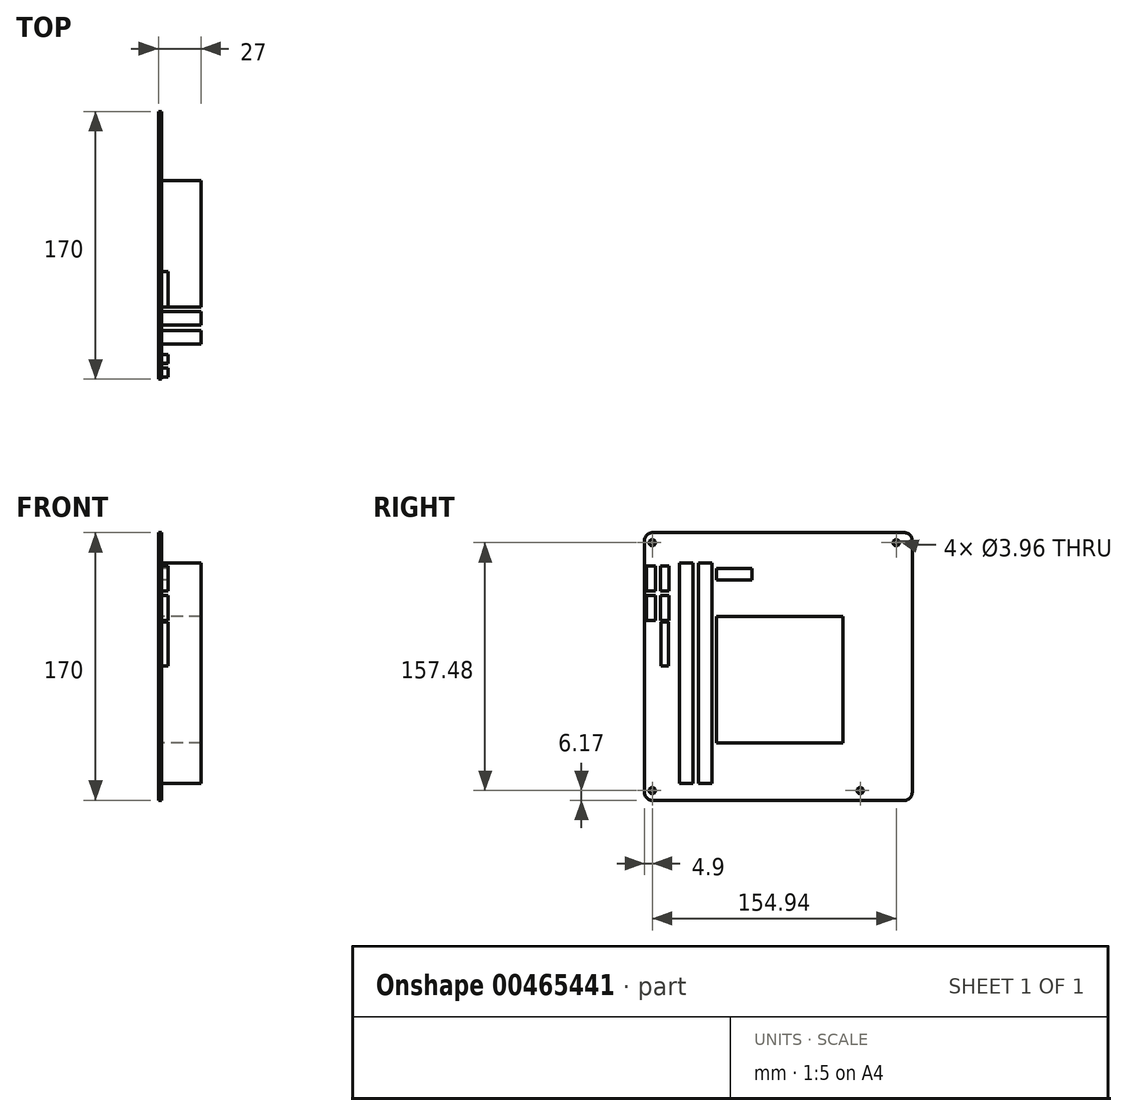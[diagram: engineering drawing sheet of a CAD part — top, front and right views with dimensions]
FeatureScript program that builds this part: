
annotation { "Feature Type Name" : "Feature", "Feature Type Description" : "" }
export const myFeature = defineFeature(function(context is Context, id is Id, definition is map)
    precondition{}
    {
        {
            var Q0;
            Q0=qCreatedBy(makeId("Right.planeOp"),FACE);
            var sketch = newSketch(context, id + "F0", { "sketchPlane" : qUnion([Q0])});
            skLineSegment(sketch, "E0.bottom", {"start": v(80, -85) * mm, "end": v(-80, -85) * mm});
            skLineSegment(sketch, "E0.top", {"start": v(80, 85) * mm, "end": v(-80, 85) * mm});
            skLineSegment(sketch, "E0.left", {"start": v(85, -80) * mm, "end": v(85, 80) * mm});
            skLineSegment(sketch, "E0.right", {"start": v(-85, -80) * mm, "end": v(-85, 80) * mm});
            skPoint(sketch, "E0.middle", {"position": v(0, 0) * mm});
            skLineSegment(sketch, "E1", {"start": v(-78.65, 78.84) * mm, "end": v(-78.65, -84.1) * mm, "construction": true});
            skLineSegment(sketch, "E2", {"start": v(-82.65, 74.84) * mm, "end": v(-47.92, 74.84) * mm, "construction": true});
            skCircle(sketch, "E3", {"center": v(-78.65, 74.84) * mm, "radius": 1.98 * mm});
            skLineSegment(sketch, "E4", {"start": v(-82.65, -80.1) * mm, "end": v(82.83, -80.1) * mm, "construction": true});
            skLineSegment(sketch, "E5", {"start": v(78.83, -84.1) * mm, "end": v(78.83, 55.98) * mm, "construction": true});
            skLineSegment(sketch, "E6", {"start": v(82.83, 51.98) * mm, "end": v(62.83, 51.98) * mm, "construction": true});
            skCircle(sketch, "E7", {"center": v(-78.65, -80.1) * mm, "radius": 1.98 * mm});
            skCircle(sketch, "E8", {"center": v(78.83, -80.1) * mm, "radius": 1.98 * mm});
            skCircle(sketch, "E9", {"center": v(78.83, 51.98) * mm, "radius": 1.98 * mm});
            skPoint(sketch, "E10.visualSharp", {"position": v(-85, -85) * mm});
            skArc(sketch, "E10.filletArc", {"start": v(-85, -80) * mm, "mid": v(-83.54, -83.54) * mm, "end": v(-80, -85) * mm});
            skPoint(sketch, "E11.visualSharp", {"position": v(85, -85) * mm});
            skArc(sketch, "E11.filletArc", {"start": v(80, -85) * mm, "mid": v(83.54, -83.54) * mm, "end": v(85, -80) * mm});
            skPoint(sketch, "E12.visualSharp", {"position": v(85, 85) * mm});
            skArc(sketch, "E12.filletArc", {"start": v(85, 80) * mm, "mid": v(83.54, 83.54) * mm, "end": v(80, 85) * mm});
            skPoint(sketch, "E13.visualSharp", {"position": v(-85, 85) * mm});
            skArc(sketch, "E13.filletArc", {"start": v(-80, 85) * mm, "mid": v(-83.54, 83.54) * mm, "end": v(-85, 80) * mm});
            skSolve(sketch);
        }
        {
            var Q0;
            Q0 = qSketchRegion(id + "F0", true);
            extrude(context, id + "F1", {"entities" : qUnion([Q0]), "depth" : 2 * mm});
        }
        {
            var Q0;
            Q0=qCreatedBy(makeId("Top.planeOp"),FACE);
            var sketch = newSketch(context, id + "F2", { "sketchPlane" : qUnion([Q0])});
            skLineSegment(sketch, "E14", {"start": v(-62.53, 0) * mm, "end": v(64.7, 0) * mm, "construction": true});
            skSolve(sketch);
        }
        {
            var Q0;
            Q0=makeQuery(id+"F1.opExtrude","SWEPT_BODY",BODY,{"disambiguationData":[OSD([sQuery(id+"F0.wireOp",EDGE,"E0.bottom"),sQuery(id+"F0.wireOp",EDGE,"E0.top"),sQuery(id+"F0.wireOp",EDGE,"E0.left"),sQuery(id+"F0.wireOp",EDGE,"E0.right"),sQuery(id+"F0.wireOp",EDGE,"E3"),sQuery(id+"F0.wireOp",EDGE,"E7"),sQuery(id+"F0.wireOp",EDGE,"E8"),sQuery(id+"F0.wireOp",EDGE,"E9"),sQuery(id+"F0.wireOp",EDGE,"E10.filletArc"),sQuery(id+"F0.wireOp",EDGE,"E11.filletArc"),sQuery(id+"F0.wireOp",EDGE,"E12.filletArc"),sQuery(id+"F0.wireOp",EDGE,"E13.filletArc")])]});
            var Q1;
            Q1=sQuery(id+"F2.wireOp",EDGE,"E14");
            transform(context, id + "F3", {"entities" : qUnion([Q0]), "transformType" : TransformType.ROTATION, "transformAxis" : qUnion([Q1]), "angle" : 90 * degree, "oppositeDirection" : true, "makeCopy" : false});
        }
        {
            var Q0;
            Q0=makeQuery(id+"F1.opExtrude","CAP_FACE",FACE,{"disambiguationData":[OSD([sQuery(id+"F0.wireOp",EDGE,"E0.bottom"),sQuery(id+"F0.wireOp",EDGE,"E0.top"),sQuery(id+"F0.wireOp",EDGE,"E0.left"),sQuery(id+"F0.wireOp",EDGE,"E0.right"),sQuery(id+"F0.wireOp",EDGE,"E3"),sQuery(id+"F0.wireOp",EDGE,"E7"),sQuery(id+"F0.wireOp",EDGE,"E8"),sQuery(id+"F0.wireOp",EDGE,"E9"),sQuery(id+"F0.wireOp",EDGE,"E10.filletArc"),sQuery(id+"F0.wireOp",EDGE,"E11.filletArc"),sQuery(id+"F0.wireOp",EDGE,"E12.filletArc"),sQuery(id+"F0.wireOp",EDGE,"E13.filletArc")])],"isStart":false});
            var sketch = newSketch(context, id + "F4", { "sketchPlane" : qUnion([Q0])});
            skLineSegment(sketch, "E15.0", {"start": v(-80, 85) * mm, "end": v(80, 85) * mm, "construction": true});
            skLineSegment(sketch, "E16.0", {"start": v(-80, -85) * mm, "end": v(80, -85) * mm, "construction": true});
            skLineSegment(sketch, "E17.0", {"start": v(-85, -80) * mm, "end": v(-85, 80) * mm, "construction": true});
            skLineSegment(sketch, "E18.bottom", {"start": v(-69.94, 28.22) * mm, "end": v(-74.55, 28.22) * mm});
            skLineSegment(sketch, "E18.top", {"start": v(-69.94, 0.5) * mm, "end": v(-74.55, 0.5) * mm});
            skLineSegment(sketch, "E18.left", {"start": v(-69.94, 28.22) * mm, "end": v(-69.94, 0.5) * mm});
            skLineSegment(sketch, "E18.right", {"start": v(-74.55, 28.22) * mm, "end": v(-74.55, 0.5) * mm});
            skLineSegment(sketch, "E19", {"start": v(-68.5, 46.63) * mm, "end": v(-83.45, 46.63) * mm, "construction": true});
            skLineSegment(sketch, "E20", {"start": v(-76.5, 64.43) * mm, "end": v(-76.5, 28.91) * mm, "construction": true});
            skLineSegment(sketch, "E21.bottom", {"start": v(-75, 47.98) * mm, "end": v(-69.36, 47.98) * mm});
            skLineSegment(sketch, "E21.top", {"start": v(-75, 63.86) * mm, "end": v(-69.36, 63.86) * mm});
            skLineSegment(sketch, "E21.left", {"start": v(-75, 47.98) * mm, "end": v(-75, 63.86) * mm});
            skLineSegment(sketch, "E21.right", {"start": v(-69.36, 47.98) * mm, "end": v(-69.36, 63.86) * mm});
            skLineSegment(sketch, "E22.MirrorCS", {"start": v(-83.64, 47.98) * mm, "end": v(-83.64, 63.86) * mm});
            skLineSegment(sketch, "E23.MirrorCS", {"start": v(-78, 63.86) * mm, "end": v(-83.64, 63.86) * mm});
            skLineSegment(sketch, "E24.MirrorCS", {"start": v(-78, 47.98) * mm, "end": v(-83.64, 47.98) * mm});
            skLineSegment(sketch, "E25.MirrorCS", {"start": v(-78, 47.98) * mm, "end": v(-78, 63.86) * mm});
            skLineSegment(sketch, "E26.MirrorCS", {"start": v(-78, 29.4) * mm, "end": v(-83.64, 29.4) * mm});
            skLineSegment(sketch, "E27.MirrorCS", {"start": v(-78, 45.28) * mm, "end": v(-83.64, 45.28) * mm});
            skLineSegment(sketch, "E28.MirrorCS", {"start": v(-75, 45.28) * mm, "end": v(-75, 29.4) * mm});
            skLineSegment(sketch, "E29.MirrorCS", {"start": v(-75, 45.28) * mm, "end": v(-69.36, 45.28) * mm});
            skLineSegment(sketch, "E30.MirrorCS", {"start": v(-69.36, 45.28) * mm, "end": v(-69.36, 29.4) * mm});
            skLineSegment(sketch, "E31.MirrorCS", {"start": v(-83.64, 45.28) * mm, "end": v(-83.64, 29.4) * mm});
            skLineSegment(sketch, "E32.MirrorCS", {"start": v(-78, 45.28) * mm, "end": v(-78, 29.4) * mm});
            skLineSegment(sketch, "E33.MirrorCS", {"start": v(-75, 29.4) * mm, "end": v(-69.36, 29.4) * mm});
            skLineSegment(sketch, "E34.bottom", {"start": v(-16.74, 55.01) * mm, "end": v(-39.27, 55.01) * mm});
            skLineSegment(sketch, "E34.top", {"start": v(-16.74, 62.4) * mm, "end": v(-39.27, 62.4) * mm});
            skLineSegment(sketch, "E34.left", {"start": v(-16.74, 55.01) * mm, "end": v(-16.74, 62.4) * mm});
            skLineSegment(sketch, "E34.right", {"start": v(-39.27, 55.01) * mm, "end": v(-39.27, 62.4) * mm});
            skLineSegment(sketch, "E35.bottom", {"start": v(41.01, 31.65) * mm, "end": v(-39.33, 31.65) * mm});
            skLineSegment(sketch, "E35.top", {"start": v(41.01, -48.47) * mm, "end": v(-39.33, -48.47) * mm});
            skLineSegment(sketch, "E35.left", {"start": v(41.01, 31.65) * mm, "end": v(41.01, -48.47) * mm});
            skLineSegment(sketch, "E35.right", {"start": v(-39.33, 31.65) * mm, "end": v(-39.33, -48.47) * mm});
            skLineSegment(sketch, "E36.bottom", {"start": v(-42.06, 65.73) * mm, "end": v(-50.68, 65.73) * mm});
            skLineSegment(sketch, "E36.top", {"start": v(-42.06, -74.29) * mm, "end": v(-50.68, -74.29) * mm});
            skLineSegment(sketch, "E36.left", {"start": v(-42.06, 65.73) * mm, "end": v(-42.06, -74.29) * mm});
            skLineSegment(sketch, "E36.right", {"start": v(-50.68, 65.73) * mm, "end": v(-50.68, -74.29) * mm});
            skLineSegment(sketch, "E37", {"start": v(-52.4, 69.79) * mm, "end": v(-52.4, -78.07) * mm, "construction": true});
            skLineSegment(sketch, "E38.MirrorCS", {"start": v(-54.11, 65.73) * mm, "end": v(-54.11, -74.29) * mm});
            skLineSegment(sketch, "E39.MirrorCS", {"start": v(-62.73, 65.73) * mm, "end": v(-54.11, 65.73) * mm});
            skLineSegment(sketch, "E40.MirrorCS", {"start": v(-62.73, 65.73) * mm, "end": v(-62.73, -74.29) * mm});
            skLineSegment(sketch, "E41.MirrorCS", {"start": v(-62.73, -74.29) * mm, "end": v(-54.11, -74.29) * mm});
            skSolve(sketch);
        }
        {
            var Q0;
            Q0=makeQuery(id+"F4.imprint","IMPRINT",FACE,{"disambiguationData":[TD([[makeQuery(id+"F4.imprint","IMPRINT",EDGE,{"derivedFrom":sQuery(id+"F4.wireOp",EDGE,"E21.bottom")}),1.0]])]});
            var Q1;
            Q1=makeQuery(id+"F4.imprint","IMPRINT",FACE,{"disambiguationData":[TD([[makeQuery(id+"F4.imprint","IMPRINT",EDGE,{"derivedFrom":sQuery(id+"F4.wireOp",EDGE,"E22.MirrorCS")}),-1.0]])]});
            var Q2;
            Q2=makeQuery(id+"F4.imprint","IMPRINT",FACE,{"disambiguationData":[TD([[makeQuery(id+"F4.imprint","IMPRINT",EDGE,{"derivedFrom":sQuery(id+"F4.wireOp",EDGE,"E26.MirrorCS")}),-1.0]])]});
            var Q3;
            Q3=makeQuery(id+"F4.imprint","IMPRINT",FACE,{"disambiguationData":[TD([[makeQuery(id+"F4.imprint","IMPRINT",EDGE,{"derivedFrom":sQuery(id+"F4.wireOp",EDGE,"E28.MirrorCS")}),1.0]])]});
            extrude(context, id + "F5", {"entities" : qUnion([Q0, Q1, Q2, Q3]), "operationType" : NewBodyOperationType.ADD, "depth" : 4 * mm});
        }
        {
            var Q0;
            Q0=makeQuery(id+"F4.imprint","IMPRINT",FACE,{"disambiguationData":[TD([[makeQuery(id+"F4.imprint","IMPRINT",EDGE,{"derivedFrom":sQuery(id+"F4.wireOp",EDGE,"E18.bottom")}),1.0]])]});
            extrude(context, id + "F6", {"entities" : qUnion([Q0]), "operationType" : NewBodyOperationType.ADD, "depth" : 4 * mm});
        }
        {
            var Q0;
            Q0=makeQuery(id+"F4.imprint","IMPRINT",FACE,{"disambiguationData":[TD([[makeQuery(id+"F4.imprint","IMPRINT",EDGE,{"derivedFrom":sQuery(id+"F4.wireOp",EDGE,"E34.bottom")}),-1.0]])]});
            extrude(context, id + "F7", {"entities" : qUnion([Q0]), "operationType" : NewBodyOperationType.ADD, "depth" : 4 * mm});
        }
        {
            var Q0;
            Q0=makeQuery(id+"F4.imprint","IMPRINT",FACE,{"disambiguationData":[TD([[makeQuery(id+"F4.imprint","IMPRINT",EDGE,{"derivedFrom":sQuery(id+"F4.wireOp",EDGE,"E35.bottom")}),1.0]])]});
            extrude(context, id + "F8", {"entities" : qUnion([Q0]), "operationType" : NewBodyOperationType.ADD, "depth" : 25 * mm});
        }
        {
            var Q0;
            Q0=makeQuery(id+"F4.imprint","IMPRINT",FACE,{"disambiguationData":[TD([[makeQuery(id+"F4.imprint","IMPRINT",EDGE,{"derivedFrom":sQuery(id+"F4.wireOp",EDGE,"E38.MirrorCS")}),-1.0]])]});
            var Q1;
            Q1=makeQuery(id+"F4.imprint","IMPRINT",FACE,{"disambiguationData":[TD([[makeQuery(id+"F4.imprint","IMPRINT",EDGE,{"derivedFrom":sQuery(id+"F4.wireOp",EDGE,"E36.bottom")}),1.0]])]});
            extrude(context, id + "F9", {"entities" : qUnion([Q0, Q1]), "operationType" : NewBodyOperationType.ADD, "depth" : 25 * mm});
        }
    });
